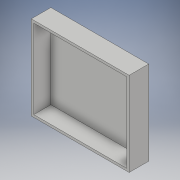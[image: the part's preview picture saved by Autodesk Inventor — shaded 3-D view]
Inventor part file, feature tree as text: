
AUTODESK INVENTOR PART (.ipt)
format: ipt  version: 2018 (Build 220112000, 112)  size: 103,424 bytes
history: native  units: in
note: dims shown in document units (in); Inventor stores cm internally (conversion verified against a paired STEP export)
features: extrude x2, sketch x2
ambient origin geometry x8: Origin, YZ Plane, XZ Plane, XY Plane, X Axis, Y Axis, Z Axis, Center Point
bodies: Solid1 (feature_tree)
feature tree (4):
  extrude  "Extrusion1"  Depth=25.81in
  extrude  "Extrusion2"  Depth=0.75in
  sketch  "Sketch1"  dims[d0=30.0in d1=25.81in]
  sketch  "Sketch2"  dims[d2=0.75in d3=0.0in d4=0.75in d5=5.25in d6=0.0in]
